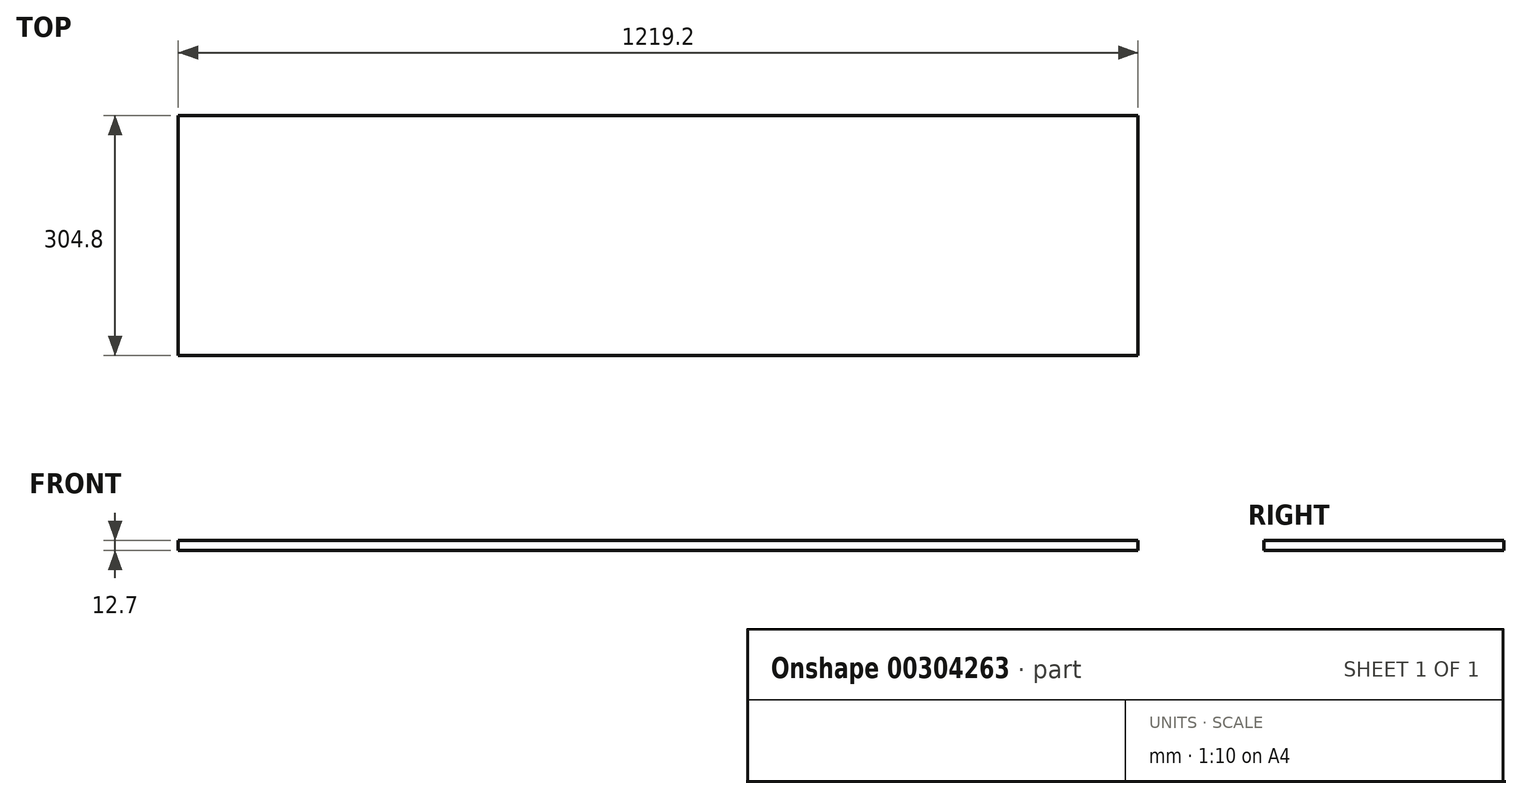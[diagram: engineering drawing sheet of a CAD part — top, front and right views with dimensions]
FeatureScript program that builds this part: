
annotation { "Feature Type Name" : "Feature", "Feature Type Description" : "" }
export const myFeature = defineFeature(function(context is Context, id is Id, definition is map)
    precondition{}
    {
        {
            var Q0;
            Q0=qCreatedBy(makeId("Top.planeOp"),FACE);
            var sketch = newSketch(context, id + "F0", { "sketchPlane" : qUnion([Q0])});
            skLineSegment(sketch, "E0.bottom", {"start": v(0, 0) * mm, "end": v(1219.2, 0) * mm});
            skLineSegment(sketch, "E0.top", {"start": v(0, 304.8) * mm, "end": v(1219.2, 304.8) * mm});
            skLineSegment(sketch, "E0.left", {"start": v(0, 0) * mm, "end": v(0, 304.8) * mm});
            skLineSegment(sketch, "E0.right", {"start": v(1219.2, 0) * mm, "end": v(1219.2, 304.8) * mm});
            skSolve(sketch);
        }
        {
            var Q0;
            Q0 = qSketchRegion(id + "F0", true);
            extrude(context, id + "F1", {"entities" : qUnion([Q0]), "depth" : 12.7 * mm});
        }
    });
